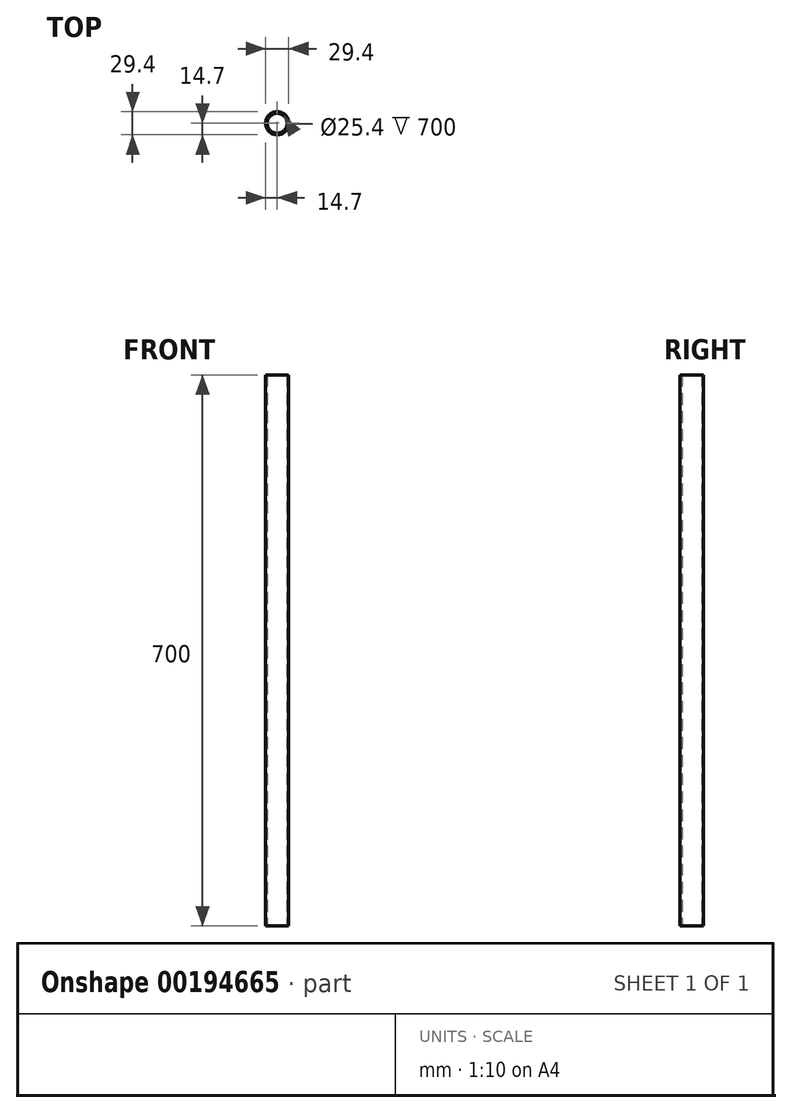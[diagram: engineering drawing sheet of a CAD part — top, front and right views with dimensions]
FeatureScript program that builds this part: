
annotation { "Feature Type Name" : "Feature", "Feature Type Description" : "" }
export const myFeature = defineFeature(function(context is Context, id is Id, definition is map)
    precondition{}
    {
        {
            var Q0;
            Q0=qCreatedBy(makeId("Top.planeOp"),FACE);
            var sketch = newSketch(context, id + "F0", { "sketchPlane" : qUnion([Q0])});
            skCircle(sketch, "E0", {"center": v(0, 0) * mm, "radius": 12.7 * mm});
            skCircle(sketch, "E1", {"center": v(0, 0) * mm, "radius": 14.7 * mm});
            skSolve(sketch);
        }
        {
            var Q0;
            Q0=makeQuery(id+"F0.imprint","IMPRINT",FACE,{"disambiguationData":[TD([[makeQuery(id+"F0.imprint","IMPRINT",EDGE,{"derivedFrom":sQuery(id+"F0.wireOp",EDGE,"E0")}),-1.0]])]});
            extrude(context, id + "F1", {"entities" : qUnion([Q0]), "depth" : 700 * mm});
        }
    });
